FCSTD DOCUMENT  (FreeCAD 1.0R39319 (Git))
Label: tampa-topo
License: All rights reserved
LicenseURL: https://en.wikipedia.org/wiki/All_rights_reserved
objects: Sketcher::SketchObject×1, PartDesign::Body×1, Part::Feature×1
note: 4 computed .brp shape members not serialized (recipe doc carries the construction recipe); baked Part::Feature solids carry a one-line shape summary decoded from their .brp

FEATURE [Sketcher::SketchObject] Sketch
  ArcFitTolerance = 1e-06
  AttachmentSupport = -> [XY_Plane]
  FullyConstrained = true
  MakeInternals = false
  MapMode = 5
  sketch-geometry (17):
    g0: LineSegment StartX=20 StartY=-42 StartZ=0 EndX=20 EndY=-30 EndZ=0
    g1: LineSegment StartX=20 StartY=-30 StartZ=0 EndX=80 EndY=-30 EndZ=0
    g2: LineSegment StartX=80 StartY=-30 StartZ=0 EndX=80 EndY=-42 EndZ=0
    g3: LineSegment StartX=80 StartY=-42 StartZ=0 EndX=20 EndY=-42 EndZ=0
    g4: GeomPoint [constr] X=50 Y=-36 Z=0
    g5: LineSegment StartX=20 StartY=-80.8 StartZ=0 EndX=20 EndY=-92.8 EndZ=0
    g6: LineSegment StartX=20 StartY=-92.8 StartZ=0 EndX=80 EndY=-92.8 EndZ=0
    g7: LineSegment StartX=80 StartY=-92.8 StartZ=0 EndX=80 EndY=-80.8 EndZ=0
    g8: LineSegment StartX=80 StartY=-80.8 StartZ=0 EndX=20 EndY=-80.8 EndZ=0
    g9: LineSegment StartX=20 StartY=-151.6 StartZ=0 EndX=20 EndY=-163.6 EndZ=0
    g10: LineSegment StartX=20 StartY=-163.6 StartZ=0 EndX=80 EndY=-163.6 EndZ=0
    g11: LineSegment StartX=80 StartY=-163.6 StartZ=0 EndX=80 EndY=-151.6 EndZ=0
    g12: LineSegment StartX=80 StartY=-151.6 StartZ=0 EndX=20 EndY=-151.6 EndZ=0
    g13: LineSegment StartX=20 StartY=-202.4 StartZ=0 EndX=20 EndY=-214.4 EndZ=0
    g14: LineSegment StartX=20 StartY=-214.4 StartZ=0 EndX=80 EndY=-214.4 EndZ=0
    g15: LineSegment StartX=80 StartY=-214.4 StartZ=0 EndX=80 EndY=-202.4 EndZ=0
    g16: LineSegment StartX=80 StartY=-202.4 StartZ=0 EndX=20 EndY=-202.4 EndZ=0
  constraints (49):
    c: Coincident(g0,g1)
    c: Coincident(g1,g2)
    c: Coincident(g2,g3)
    c: Coincident(g3,g0)
    c: Vertical(g0)
    c: Vertical(g2)
    c: Horizontal(g1)
    c: Horizontal(g3)
    c: Symmetric(g2,g0,g4)
    c: DistanceY(g4,g-1) = 36
    c: DistanceX(g3,g3) = 60
    c: DistanceX(g-1,g0) = 20
    c: Coincident(g5,g6)
    c: Coincident(g6,g7)
    c: Coincident(g7,g8)
    c: Coincident(g8,g5)
    c: Vertical(g5)
    c: Vertical(g7)
    c: Horizontal(g6)
    c: Horizontal(g8)
    c: Coincident(g9,g10)
    c: Coincident(g10,g11)
    c: Coincident(g11,g12)
    c: Coincident(g12,g9)
    c: Vertical(g9)
    c: Vertical(g11)
    c: Horizontal(g10)
    c: Horizontal(g12)
    c: Coincident(g13,g14)
    c: Coincident(g14,g15)
    c: Coincident(g15,g16)
    c: Coincident(g16,g13)
    c: Vertical(g13)
    c: Vertical(g15)
    c: Horizontal(g14)
    c: Horizontal(g16)
    c: Equal(g3,g8)
    c: Equal(g6,g12)
    c: Equal(g10,g16)
    c: Equal(g15,g11)
    c: Equal(g9,g5)
    c: Equal(g7,g2)
    c: Vertical(g0,g5)
    c: Vertical(g5,g9)
    c: Vertical(g9,g13)
    c: DistanceY(g7,g1) = 50.8
    c: DistanceY(g15,g11) = 50.8
    c: DistanceY(g2,g2) = 12
    c: DistanceY(g11,g7) = 70.8
FEATURE [PartDesign::Body] Body
  AllowCompound = false
  Group = -> [Sketch]
  Origin = -> Origin
FEATURE [Part::Feature] path4
  shape: bbox 276.2 x 276.2 x 2e-07 mm, 0 faces, 0 solids (baked)
